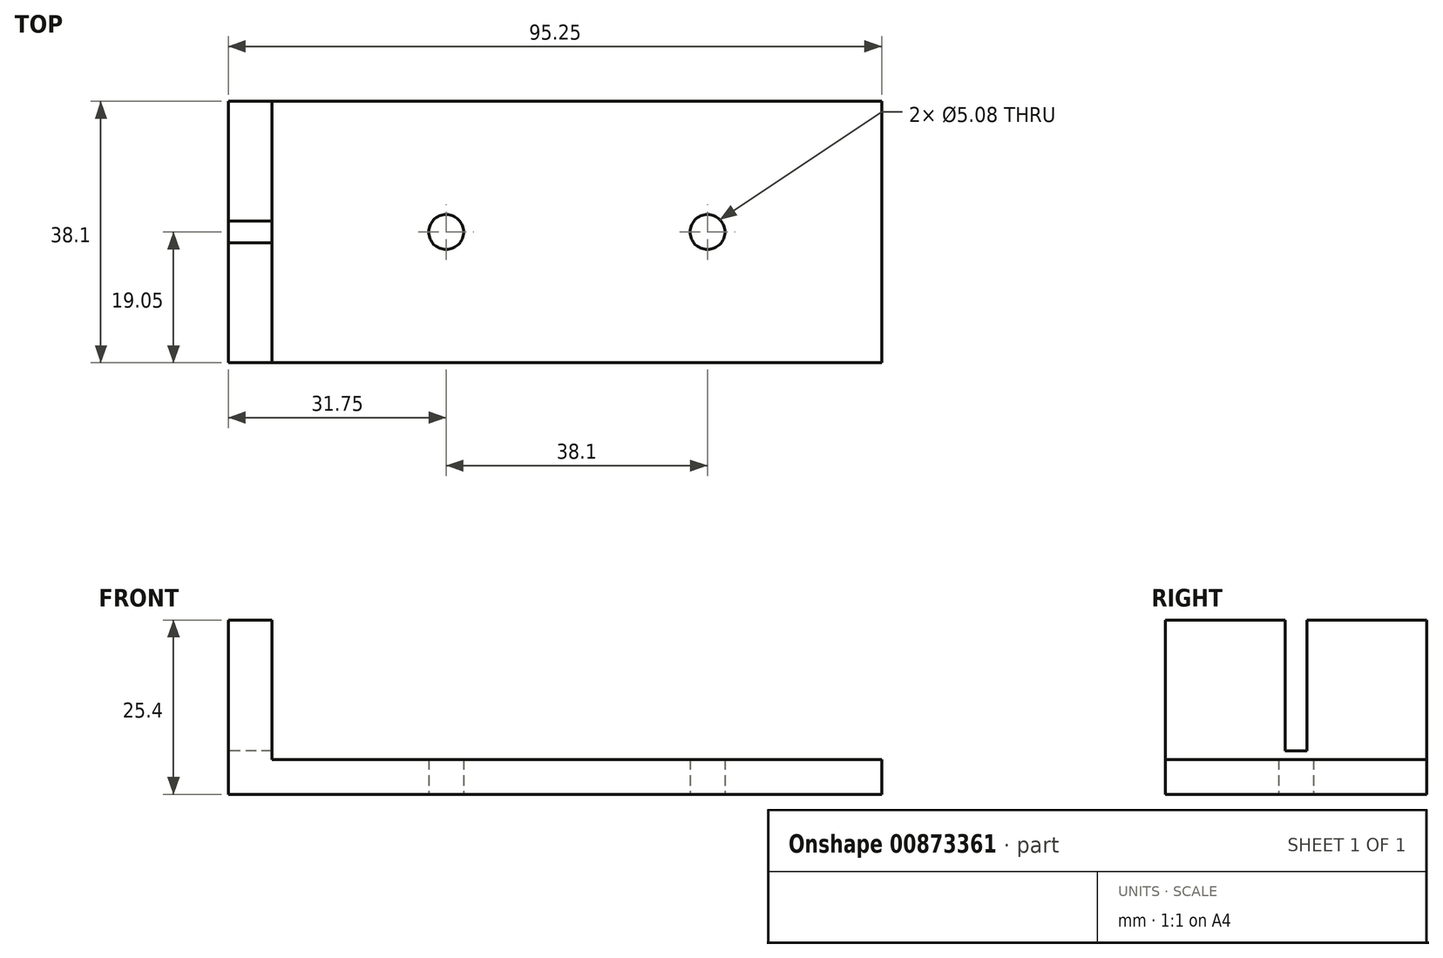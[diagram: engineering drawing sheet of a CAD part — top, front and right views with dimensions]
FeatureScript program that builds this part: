
annotation { "Feature Type Name" : "Feature", "Feature Type Description" : "" }
export const myFeature = defineFeature(function(context is Context, id is Id, definition is map)
    precondition{}
    {
        {
            var Q0;
            Q0=qCreatedBy(makeId("Top.planeOp"),FACE);
            var sketch = newSketch(context, id + "F0", { "sketchPlane" : qUnion([Q0])});
            skLineSegment(sketch, "E0.bottom", {"start": v(0, 0) * mm, "end": v(95.25, 0) * mm});
            skLineSegment(sketch, "E0.top", {"start": v(0, 38.1) * mm, "end": v(95.25, 38.1) * mm});
            skLineSegment(sketch, "E0.left", {"start": v(0, 0) * mm, "end": v(0, 38.1) * mm});
            skLineSegment(sketch, "E0.right", {"start": v(95.25, 0) * mm, "end": v(95.25, 38.1) * mm});
            skCircle(sketch, "E1", {"center": v(69.85, 19.05) * mm, "radius": 2.54 * mm});
            skCircle(sketch, "E2", {"center": v(31.75, 19.05) * mm, "radius": 2.54 * mm});
            skPoint(sketch, "E2.centerSnap0", {"position": v(0, 19.05) * mm});
            skSolve(sketch);
        }
        {
            var Q0;
            Q0 = qSketchRegion(id + "F0", true);
            extrude(context, id + "F1", {"entities" : qUnion([Q0]), "depth" : 25.4 * mm, "offsetDistance" : 25.4 * mm});
        }
        {
            var Q0;
            Q0=makeQuery(id+"F1.opExtrude","SWEPT_FACE",FACE,{"disambiguationData":[OSD([sQuery(id+"F0.wireOp",EDGE,"E0.bottom")])]});
            var sketch = newSketch(context, id + "F2", { "sketchPlane" : qUnion([Q0])});
            skLineSegment(sketch, "E3.bottom", {"start": v(6.35, 25.4) * mm, "end": v(95.25, 25.4) * mm});
            skLineSegment(sketch, "E3.top", {"start": v(6.35, 5.08) * mm, "end": v(95.25, 5.08) * mm});
            skLineSegment(sketch, "E3.left", {"start": v(6.35, 25.4) * mm, "end": v(6.35, 5.08) * mm});
            skLineSegment(sketch, "E3.right", {"start": v(95.25, 25.4) * mm, "end": v(95.25, 5.08) * mm});
            skSolve(sketch);
        }
        {
            var Q0;
            Q0 = qSketchRegion(id + "F2", true);
            extrude(context, id + "F3", {"entities" : qUnion([Q0]), "operationType" : NewBodyOperationType.REMOVE, "endBound" : BoundingType.THROUGH_ALL, "oppositeDirection" : true, "depth" : 25.4 * mm, "offsetDistance" : 25.4 * mm});
        }
        {
            var Q0;
            Q0=makeQuery(id+"F1.opExtrude","SWEPT_FACE",FACE,{"disambiguationData":[OSD([sQuery(id+"F0.wireOp",EDGE,"E0.left")])]});
            var sketch = newSketch(context, id + "F4", { "sketchPlane" : qUnion([Q0])});
            skLineSegment(sketch, "E4.bottom", {"start": v(-20.64, 25.4) * mm, "end": v(-17.46, 25.4) * mm});
            skLineSegment(sketch, "E4.top", {"start": v(-20.64, 6.35) * mm, "end": v(-17.46, 6.35) * mm});
            skLineSegment(sketch, "E4.left", {"start": v(-20.64, 25.4) * mm, "end": v(-20.64, 6.35) * mm});
            skLineSegment(sketch, "E4.right", {"start": v(-17.46, 25.4) * mm, "end": v(-17.46, 6.35) * mm});
            skSolve(sketch);
        }
        {
            var Q0;
            Q0 = qSketchRegion(id + "F4", true);
            extrude(context, id + "F5", {"entities" : qUnion([Q0]), "operationType" : NewBodyOperationType.REMOVE, "oppositeDirection" : true, "depth" : 25.4 * mm, "offsetDistance" : 25.4 * mm});
        }
    });
